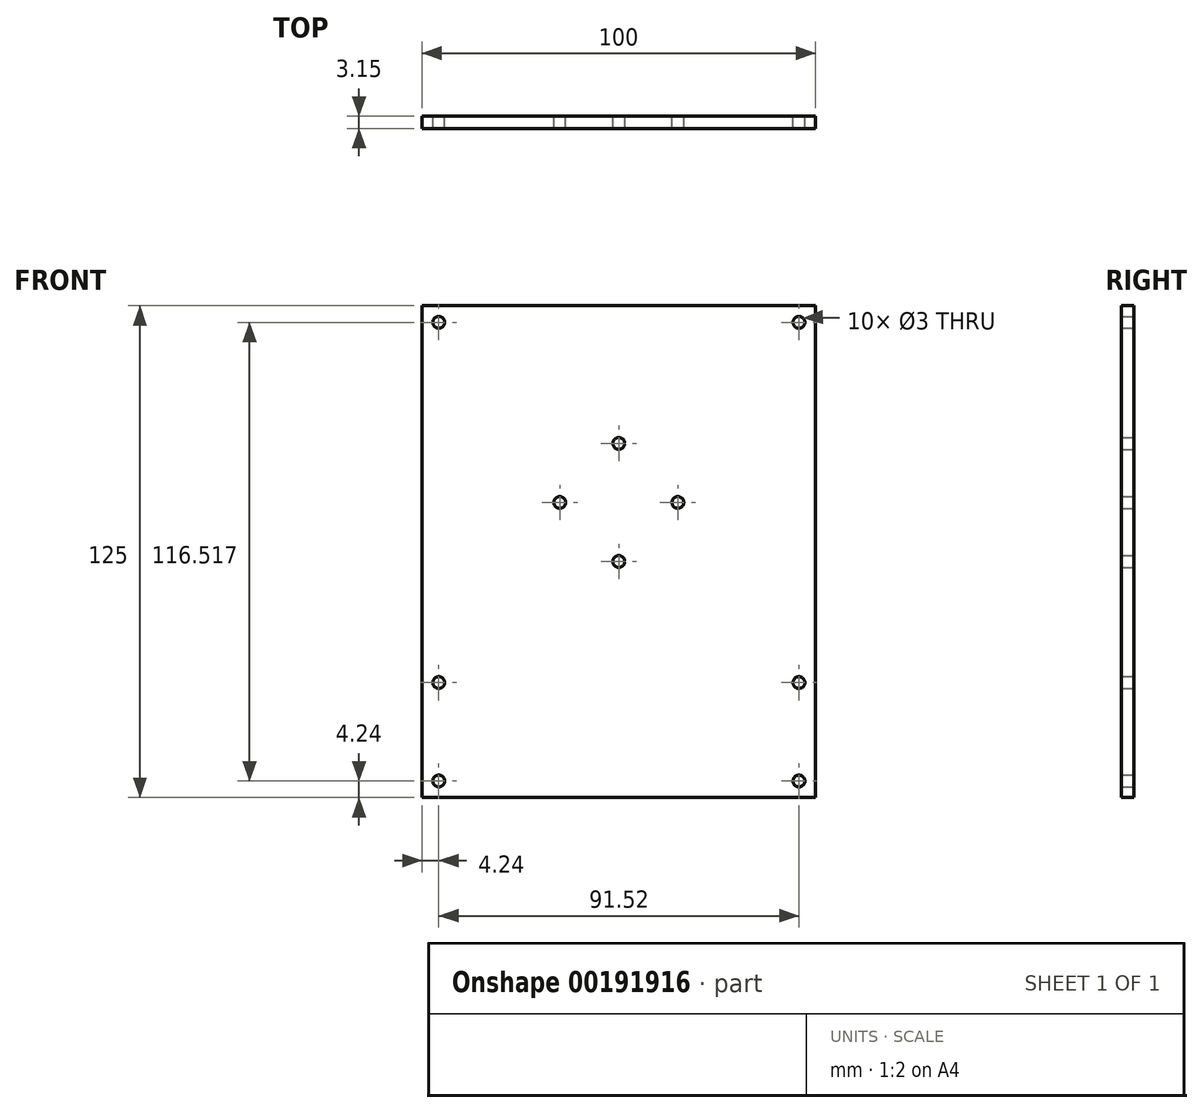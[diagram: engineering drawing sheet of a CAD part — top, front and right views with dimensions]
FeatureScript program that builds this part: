
annotation { "Feature Type Name" : "Feature", "Feature Type Description" : "" }
export const myFeature = defineFeature(function(context is Context, id is Id, definition is map)
    precondition{}
    {
        {
            var Q0;
            Q0=qCreatedBy(makeId("Front.planeOp"),FACE);
            var sketch = newSketch(context, id + "F0", { "sketchPlane" : qUnion([Q0])});
            skLineSegment(sketch, "E0.bottom", {"start": v(50, 50) * mm, "end": v(-50, 50) * mm});
            skLineSegment(sketch, "E0.top", {"start": v(50, -50) * mm, "end": v(-50, -50) * mm, "construction": true});
            skLineSegment(sketch, "E0.left", {"start": v(50, 50) * mm, "end": v(50, -50) * mm});
            skLineSegment(sketch, "E0.right", {"start": v(-50, 50) * mm, "end": v(-50, -50) * mm});
            skPoint(sketch, "E0.middle", {"position": v(0, 0) * mm});
            skCircle(sketch, "E1", {"center": v(0, 0) * mm, "radius": 15 * mm, "construction": true});
            skCircle(sketch, "E2", {"center": v(0, 15) * mm, "radius": 1.5 * mm});
            skCircle(sketch, "E3.1.0", {"center": v(-15, 0) * mm, "radius": 1.5 * mm});
            skCircle(sketch, "E3.2.0", {"center": v(0, -15) * mm, "radius": 1.5 * mm});
            skCircle(sketch, "E3.3.0", {"center": v(15, 0) * mm, "radius": 1.5 * mm});
            skLineSegment(sketch, "E4", {"start": v(-50, -50) * mm, "end": v(50, 50) * mm, "construction": true});
            skLineSegment(sketch, "E5", {"start": v(-50, 50) * mm, "end": v(50, -50) * mm, "construction": true});
            skCircle(sketch, "E6", {"center": v(45.76, 45.76) * mm, "radius": 1.5 * mm});
            skCircle(sketch, "E7", {"center": v(-45.76, 45.76) * mm, "radius": 1.5 * mm});
            skCircle(sketch, "E8", {"center": v(-45.76, -45.76) * mm, "radius": 1.5 * mm});
            skCircle(sketch, "E9", {"center": v(45.76, -45.76) * mm, "radius": 1.5 * mm});
            skLineSegment(sketch, "E10", {"start": v(-50, -50) * mm, "end": v(-50, -75) * mm});
            skLineSegment(sketch, "E11", {"start": v(-50, -75) * mm, "end": v(50, -75) * mm});
            skLineSegment(sketch, "E12", {"start": v(50, -75) * mm, "end": v(50, -50) * mm});
            skCircle(sketch, "E13", {"center": v(45.76, -70.76) * mm, "radius": 1.5 * mm});
            skCircle(sketch, "E14", {"center": v(-45.76, -70.76) * mm, "radius": 1.5 * mm});
            skSolve(sketch);
        }
        {
            var Q0;
            Q0=makeQuery(id+"F0.imprint","IMPRINT",FACE,{"disambiguationData":[TD([[makeQuery(id+"F0.imprint","IMPRINT",EDGE,{"derivedFrom":sQuery(id+"F0.wireOp",EDGE,"E0.bottom")}),1.0]])]});
            extrude(context, id + "F1", {"entities" : qUnion([Q0]), "depth" : 3.15 * mm});
        }
    });
